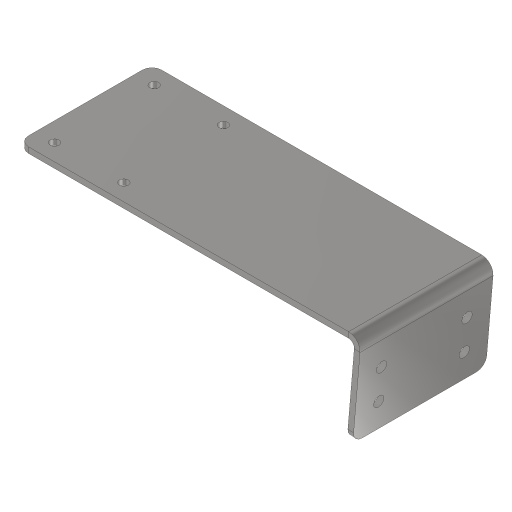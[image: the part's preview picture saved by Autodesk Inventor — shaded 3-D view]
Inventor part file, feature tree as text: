
AUTODESK INVENTOR PART (.ipt)
format: ipt  version: 2024.3 (Build 283343000, 343)  size: 216,576 bytes
history: native  units: mm
features: sheet_metal_op x4, sketch x4, other x3, hole x2, fillet x1, projected_geometry x1
ambient origin geometry x8: Origin, YZ Plane, XZ Plane, XY Plane, X Axis, Y Axis, Z Axis, Center Point
bodies: Solid1 (feature_tree)
feature tree (15):
  sheet_metal_op  "Face1"
  sheet_metal_op  "Flange1"
  hole  "Hole1"  [1 undecoded]
  hole  "Hole2"  [1 undecoded]
  fillet  "Fillet1"  Radius=1.5mm
  sketch  "Sketch1"  dims[d0=70.0mm d1=180.0mm]
  other  "Plate1"
  sketch  "Sketch2"  dims[d2=3.0mm d3=3.0mm d4=1.5mm]
  other  "Plate2"
  sheet_metal_op  "Bend1"
  sheet_metal_op  "Corner1"
  sketch  "Sketch3"  dims[d5=6.0mm]
  sketch  "Sketch4"  dims[d6=3.0mm d7=50.0mm d8=16.580628mm d9=3.0mm d10=12.0mm d11=3.0mm d12=3.0mm d13=52.4mm d14=36.4mm d15=10.0mm d16=4.8mm d17=6.0mm d18=9.4mm d19=2.0mm d20=90.0deg d21=3.0mm d22=0.0mm d23=0.0mm d24=70.0mm d25=45.0mm d26=13.5mm d27=16.452149mm d28=5.5mm d29=10.75mm d30=5.5mm d31=6.0mm d32=10.4mm d33=2.0mm d34=90.0deg d35=3.0mm d36=20.594885mm d37=5.0mm]
  projected_geometry  "Projected Loop1"
  other  "Definition1"
note: 2 required parameter values undecoded (feature->parameter linkage not recoverable at this tier; creation-order binding heuristic only, values carry confidence <= 0.55)
